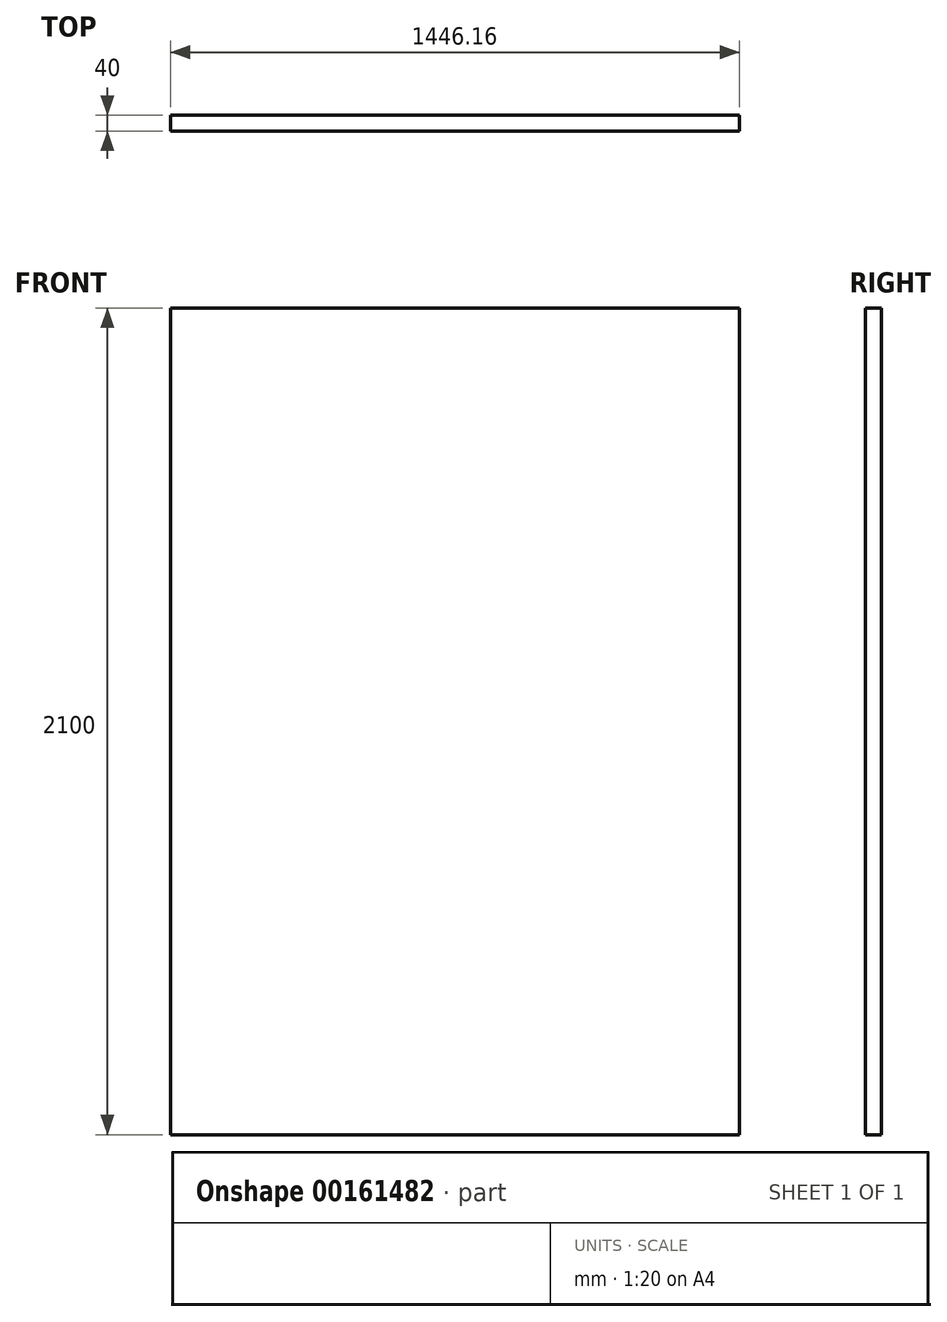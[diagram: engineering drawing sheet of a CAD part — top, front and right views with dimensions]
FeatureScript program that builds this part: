
annotation { "Feature Type Name" : "Feature", "Feature Type Description" : "" }
export const myFeature = defineFeature(function(context is Context, id is Id, definition is map)
    precondition{}
    {
        {
            var Q0;
            Q0=qCreatedBy(makeId("Front.planeOp"),FACE);
            var sketch = newSketch(context, id + "F0", { "sketchPlane" : qUnion([Q0])});
            skLineSegment(sketch, "E0.bottom", {"start": v(-723.08, 1050) * mm, "end": v(723.08, 1050) * mm});
            skLineSegment(sketch, "E0.top", {"start": v(-723.08, -1050) * mm, "end": v(723.08, -1050) * mm});
            skLineSegment(sketch, "E0.left", {"start": v(-723.08, 1050) * mm, "end": v(-723.08, -1050) * mm});
            skLineSegment(sketch, "E0.right", {"start": v(723.08, 1050) * mm, "end": v(723.08, -1050) * mm});
            skPoint(sketch, "E0.middle", {"position": v(0, 0) * mm});
            skSolve(sketch);
        }
        {
            var Q0;
            Q0 = qSketchRegion(id + "F0", true);
            extrude(context, id + "F1", {"entities" : qUnion([Q0]), "endBound" : BoundingType.SYMMETRIC, "depth" : 40 * mm, "offsetDistance" : 25 * mm});
        }
    });
